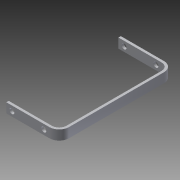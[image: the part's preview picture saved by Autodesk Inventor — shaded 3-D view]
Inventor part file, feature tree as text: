
AUTODESK INVENTOR PART (.ipt)
format: ipt  version: 2013 (Build 170138000, 138)  size: 123,392 bytes
history: native  units: in
note: dims shown in document units (in); Inventor stores cm internally (conversion verified against a paired STEP export)
features: sheet_metal_op x7, sketch x4, other x3, extrude x1
ambient origin geometry x8: Origin, YZ Plane, XZ Plane, XY Plane, X Axis, Y Axis, Z Axis, Center Point
bodies: Solid1 (feature_tree)
feature tree (15):
  sheet_metal_op  "Face1"
  sheet_metal_op  "Flange2"
  sheet_metal_op  "Flange3"
  extrude  "Extrusion1"  Depth=0.5in
  sketch  "Sketch1"  dims[d1=2.244in d2=0.5in]
  other  "Plate1"
  sketch  "Sketch3"  dims[d3=0.295in]
  other  "Plate3"
  sheet_metal_op  "Bend2"
  sheet_metal_op  "Corner2"
  sketch  "Sketch4"  dims[d4=0.25in]
  other  "Plate4"
  sheet_metal_op  "Bend3"
  sheet_metal_op  "Corner3"
  sketch  "Sketch5"  dims[d5=0.295in d6=0.26in d7=0.26in d8=0.125in d19=0.25in d20=0.125in d21=0.0625in d22=0.25in d23=0.125in d24=5.447in d25=90.0deg d26=0.375in d27=0.5in d28=0.125in d29=0.125in d30=0.125in d31=0.0625in d32=0.25in d33=0.125in d34=2.744in d35=90.0deg d36=0.375in d37=0.5in d38=0.125in d39=0.125in d40=90.0in d41=0.0in]
